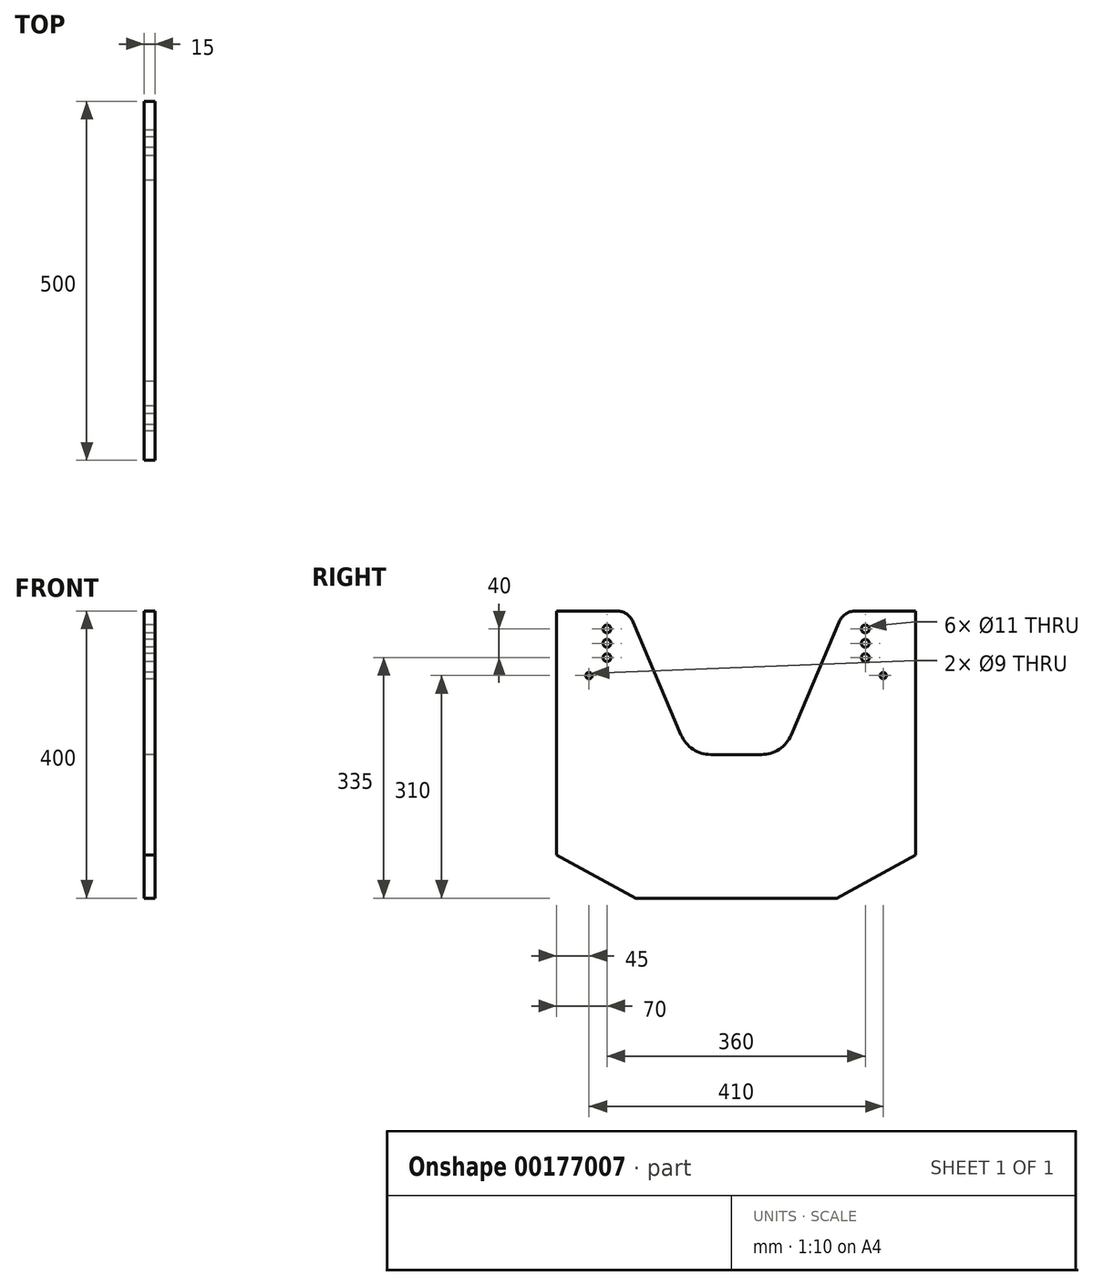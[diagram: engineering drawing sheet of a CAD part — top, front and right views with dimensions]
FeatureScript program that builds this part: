
annotation { "Feature Type Name" : "Feature", "Feature Type Description" : "" }
export const myFeature = defineFeature(function(context is Context, id is Id, definition is map)
    precondition{}
    {
        {
            var Q0;
            Q0=qCreatedBy(makeId("Right.planeOp"),FACE);
            var sketch = newSketch(context, id + "F0", { "sketchPlane" : qUnion([Q0])});
            skLineSegment(sketch, "E0.bottom", {"start": v(-250, 155) * mm, "end": v(-166.54, 155) * mm});
            skLineSegment(sketch, "E0.top", {"start": v(-140, -245) * mm, "end": v(0, -245) * mm});
            skLineSegment(sketch, "E0.left", {"start": v(-250, 155) * mm, "end": v(-250, -185) * mm});
            skLineSegment(sketch, "E0.right", {"start": v(0, 155) * mm, "end": v(0, -245) * mm, "construction": true});
            skLineSegment(sketch, "E1", {"start": v(-180, 155) * mm, "end": v(-180, 16.92) * mm, "construction": true});
            skCircle(sketch, "E2", {"center": v(-180, 130) * mm, "radius": 5.5 * mm});
            skCircle(sketch, "E3", {"center": v(-180, 110) * mm, "radius": 5.5 * mm});
            skCircle(sketch, "E4", {"center": v(-180, 90) * mm, "radius": 5.5 * mm});
            skCircle(sketch, "E5", {"center": v(-205, 65) * mm, "radius": 4.5 * mm});
            skLineSegment(sketch, "E6", {"start": v(-250, -185) * mm, "end": v(-140, -245) * mm});
            skLineSegment(sketch, "E7", {"start": v(-143.53, 139.78) * mm, "end": v(-76.64, -17.6) * mm});
            skArc(sketch, "E8", {"start": v(-143.53, 139.78) * mm, "mid": v(-152.75, 150.85) * mm, "end": v(-166.54, 155) * mm});
            skArc(sketch, "E9", {"start": v(-76.64, -17.6) * mm, "mid": v(-60.06, -37.53) * mm, "end": v(-35.23, -45) * mm});
            skPoint(sketch, "E10.orphan", {"position": v(-150, 155) * mm});
            skPoint(sketch, "E11.orphan", {"position": v(-65, -45) * mm});
            skLineSegment(sketch, "E12.trimOffspring", {"start": v(-35.23, -45) * mm, "end": v(0, -45) * mm});
            skPoint(sketch, "E13.start.orphan", {"position": v(-250, -45) * mm});
            skPoint(sketch, "E14.end.orphan", {"position": v(0, -185) * mm});
            skPoint(sketch, "E15.orphan", {"position": v(-250, -245) * mm});
            skLineSegment(sketch, "E16.MirrorCS", {"start": v(140, -245) * mm, "end": v(0, -245) * mm});
            skLineSegment(sketch, "E17.MirrorCS", {"start": v(250, -185) * mm, "end": v(140, -245) * mm});
            skLineSegment(sketch, "E18.MirrorCS", {"start": v(250, 155) * mm, "end": v(250, -185) * mm});
            skLineSegment(sketch, "E19.MirrorCS", {"start": v(250, 155) * mm, "end": v(166.54, 155) * mm});
            skPoint(sketch, "E20.MirrorP", {"position": v(150, 155) * mm});
            skLineSegment(sketch, "E21.MirrorCS", {"start": v(143.53, 139.78) * mm, "end": v(76.64, -17.6) * mm});
            skArc(sketch, "E22.MirrorCS", {"start": v(143.53, 139.78) * mm, "mid": v(152.75, 150.85) * mm, "end": v(166.54, 155) * mm});
            skArc(sketch, "E23.MirrorCS", {"start": v(76.64, -17.6) * mm, "mid": v(60.06, -37.53) * mm, "end": v(35.23, -45) * mm});
            skLineSegment(sketch, "E24.MirrorCS", {"start": v(35.23, -45) * mm, "end": v(0, -45) * mm});
            skCircle(sketch, "E25.MirrorC", {"center": v(180, 130) * mm, "radius": 5.5 * mm});
            skCircle(sketch, "E26.MirrorC", {"center": v(180, 110) * mm, "radius": 5.5 * mm});
            skCircle(sketch, "E27.MirrorC", {"center": v(180, 90) * mm, "radius": 5.5 * mm});
            skCircle(sketch, "E28.MirrorC", {"center": v(205, 65) * mm, "radius": 4.5 * mm});
            skSolve(sketch);
        }
        {
            var Q0;
            Q0=makeQuery(id+"F0.imprint","IMPRINT",FACE,{"disambiguationData":[TD([[makeQuery(id+"F0.imprint","IMPRINT",EDGE,{"derivedFrom":sQuery(id+"F0.wireOp",EDGE,"E0.bottom")}),-1.0]])]});
            extrude(context, id + "F1", {"entities" : qUnion([Q0]), "depth" : 15 * mm});
        }
    });
